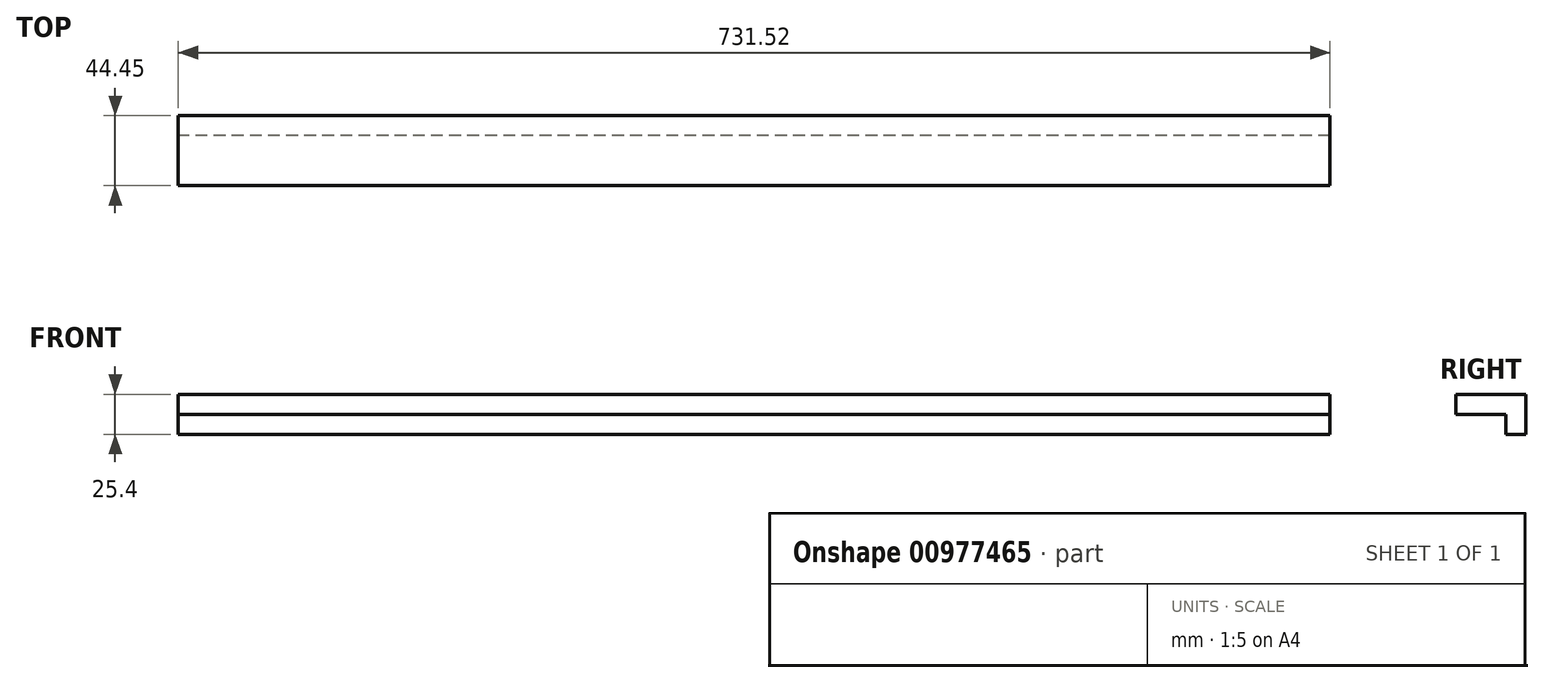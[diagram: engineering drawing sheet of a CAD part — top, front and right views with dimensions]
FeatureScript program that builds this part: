
annotation { "Feature Type Name" : "Feature", "Feature Type Description" : "" }
export const myFeature = defineFeature(function(context is Context, id is Id, definition is map)
    precondition{}
    {
        {
            var Q0;
            Q0=qCreatedBy(makeId("Right.planeOp"),FACE);
            var sketch = newSketch(context, id + "F0", { "sketchPlane" : qUnion([Q0])});
            skLineSegment(sketch, "E0", {"start": v(0, 0) * mm, "end": v(0, -12.7) * mm});
            skLineSegment(sketch, "E1", {"start": v(0, -12.7) * mm, "end": v(12.7, -12.7) * mm});
            skLineSegment(sketch, "E2", {"start": v(12.7, -12.7) * mm, "end": v(12.7, 12.7) * mm});
            skLineSegment(sketch, "E3", {"start": v(12.7, 12.7) * mm, "end": v(-31.75, 12.7) * mm});
            skLineSegment(sketch, "E4", {"start": v(-31.75, 12.7) * mm, "end": v(-31.75, 0) * mm});
            skLineSegment(sketch, "E5", {"start": v(-31.75, 0) * mm, "end": v(0, 0) * mm});
            skSolve(sketch);
        }
        {
            var Q0;
            Q0=makeQuery(id+"F0.imprint","IMPRINT",FACE,{"disambiguationData":[TD([[makeQuery(id+"F0.imprint","IMPRINT",EDGE,{"derivedFrom":sQuery(id+"F0.wireOp",EDGE,"E0")}),1.0]])]});
            extrude(context, id + "F1", {"entities" : qUnion([Q0]), "endBound" : BoundingType.SYMMETRIC, "depth" : 731.52 * mm, "offsetDistance" : 25.4 * mm});
        }
    });
